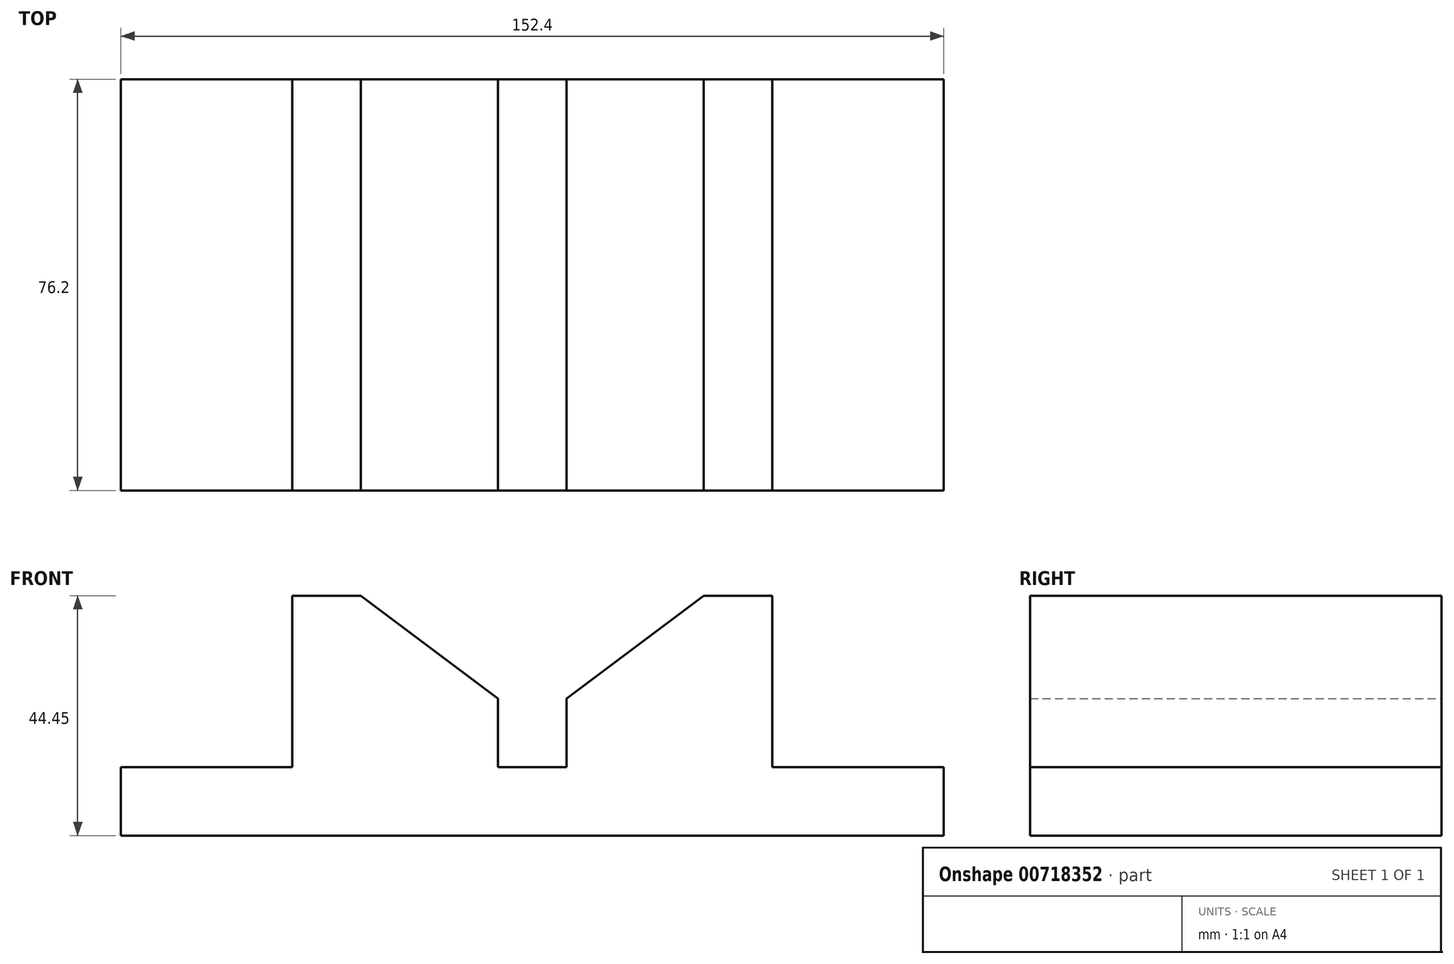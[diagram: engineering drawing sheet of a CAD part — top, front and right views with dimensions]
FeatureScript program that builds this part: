
annotation { "Feature Type Name" : "Feature", "Feature Type Description" : "" }
export const myFeature = defineFeature(function(context is Context, id is Id, definition is map)
    precondition{}
    {
        {
            var Q0;
            Q0=qCreatedBy(makeId("Front.planeOp"),FACE);
            var sketch = newSketch(context, id + "F0", { "sketchPlane" : qUnion([Q0])});
            skLineSegment(sketch, "E0", {"start": v(-70.92, -20.32) * mm, "end": v(81.48, -20.32) * mm});
            skLineSegment(sketch, "E1", {"start": v(81.48, -20.32) * mm, "end": v(81.48, -7.62) * mm});
            skLineSegment(sketch, "E2", {"start": v(81.48, -7.62) * mm, "end": v(49.73, -7.62) * mm});
            skLineSegment(sketch, "E3", {"start": v(49.73, -7.62) * mm, "end": v(49.73, 24.13) * mm});
            skLineSegment(sketch, "E4", {"start": v(49.73, 24.13) * mm, "end": v(37.03, 24.13) * mm});
            skLineSegment(sketch, "E5", {"start": v(-26.47, 24.13) * mm, "end": v(-39.17, 24.13) * mm});
            skLineSegment(sketch, "E6", {"start": v(-39.17, 24.13) * mm, "end": v(-39.17, -7.62) * mm});
            skLineSegment(sketch, "E7", {"start": v(-39.17, -7.62) * mm, "end": v(-70.92, -7.62) * mm});
            skLineSegment(sketch, "E8", {"start": v(-70.92, -7.62) * mm, "end": v(-70.92, -20.32) * mm});
            skLineSegment(sketch, "E9", {"start": v(11.63, 5.08) * mm, "end": v(11.63, -7.62) * mm});
            skLineSegment(sketch, "E10", {"start": v(11.63, -7.62) * mm, "end": v(-1.07, -7.62) * mm});
            skLineSegment(sketch, "E11", {"start": v(-1.07, -7.62) * mm, "end": v(-1.07, 5.08) * mm});
            skLineSegment(sketch, "E12", {"start": v(11.63, 5.08) * mm, "end": v(37.03, 24.13) * mm});
            skLineSegment(sketch, "E13", {"start": v(-26.47, 24.13) * mm, "end": v(-1.07, 5.08) * mm});
            skSolve(sketch);
        }
        {
            var Q0;
            Q0 = qSketchRegion(id + "F0", true);
            extrude(context, id + "F1", {"entities" : qUnion([Q0]), "depth" : 76.2 * mm, "offsetDistance" : 25.4 * mm});
        }
    });
